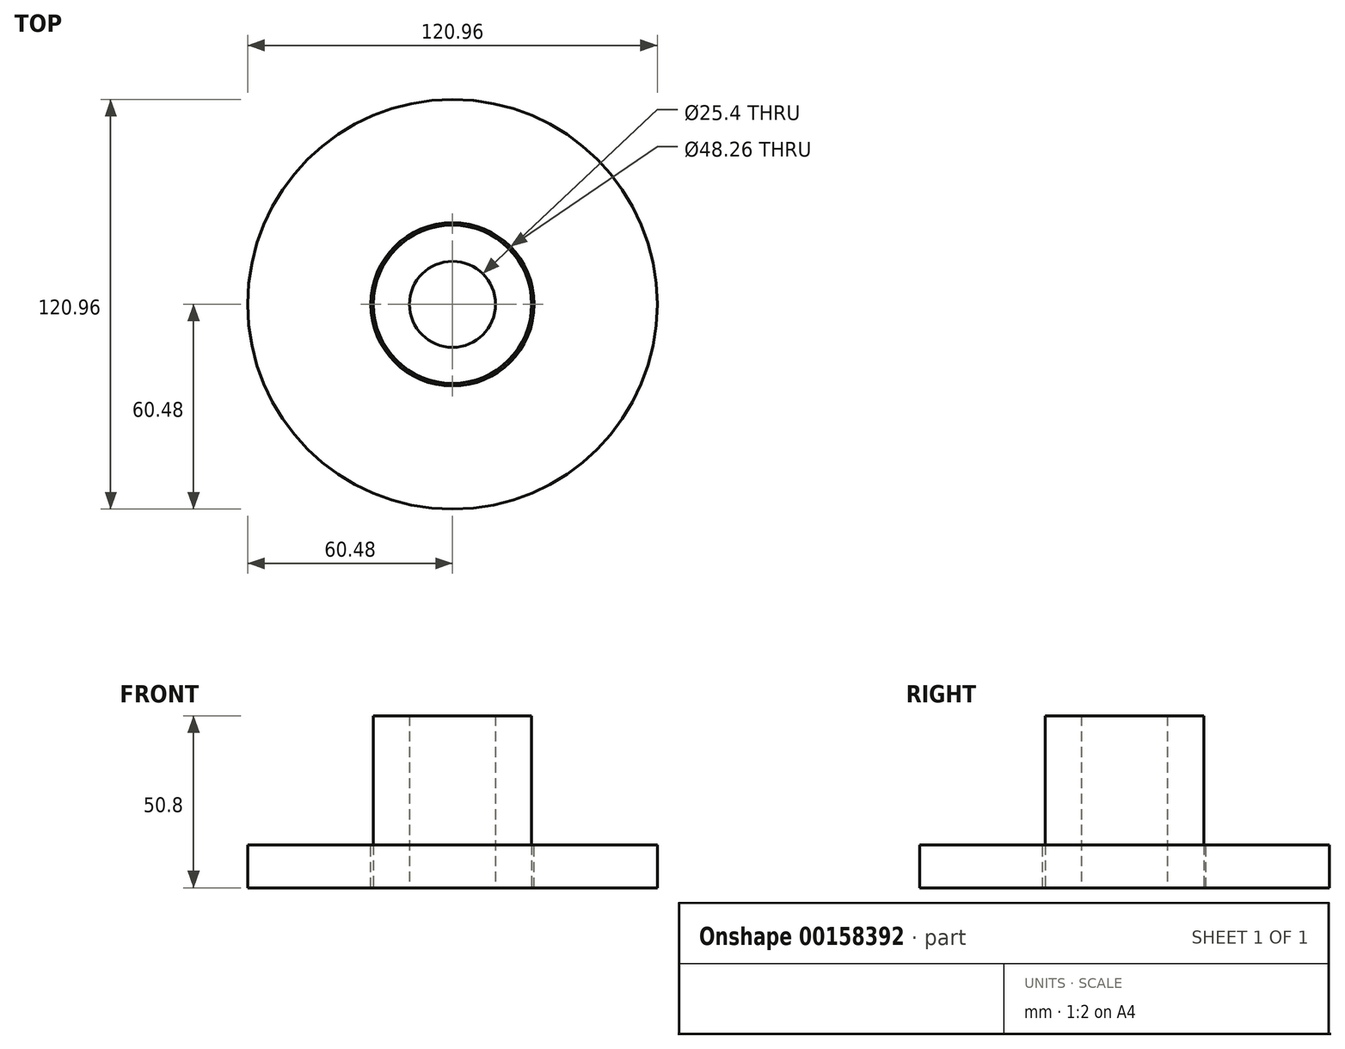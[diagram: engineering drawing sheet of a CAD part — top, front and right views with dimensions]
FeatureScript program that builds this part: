
annotation { "Feature Type Name" : "Feature", "Feature Type Description" : "" }
export const myFeature = defineFeature(function(context is Context, id is Id, definition is map)
    precondition{}
    {
        {
            var Q0;
            Q0=qCreatedBy(makeId("Top.planeOp"),FACE);
            var sketch = newSketch(context, id + "F0", { "sketchPlane" : qUnion([Q0])});
            skCircle(sketch, "E0", {"center": v(0, 0) * mm, "radius": 60.48 * mm});
            skSolve(sketch);
        }
        {
            var Q0;
            Q0 = qSketchRegion(id + "F0", true);
            extrude(context, id + "F1", {"entities" : qUnion([Q0]), "depth" : 12.7 * mm});
        }
        {
            var Q0;
            Q0=makeQuery(id+"F1.opExtrude","CAP_FACE",FACE,{"disambiguationData":[OSD([sQuery(id+"F0.wireOp",EDGE,"E0")])],"isStart":false});
            var sketch = newSketch(context, id + "F2", { "sketchPlane" : qUnion([Q0])});
            skCircle(sketch, "E1", {"center": v(0, 0) * mm, "radius": 8.5 * mm});
            skSolve(sketch);
        }
        {
            var Q0;
            Q0=sQuery(id+"F2.wireOp",VERTEX,"E1.center");
            var Q1;
            Q1=makeQuery(id+"F1.opExtrude","SWEPT_BODY",BODY,{"disambiguationData":[OSD([sQuery(id+"F0.wireOp",EDGE,"E0")])]});
            hole(context, id + "F3", {"style" : HoleStyle.SIMPLE, "endStyle" : HoleEndStyle.THROUGH, "holeDiameter" : 48.26 * mm, "locations" : qUnion([Q0]), "scope" : qUnion([Q1]), "isTappedThrough" : true});
        }
        {
            var Q0;
            Q0=qCreatedBy(makeId("Top.planeOp"),FACE);
            var sketch = newSketch(context, id + "F4", { "sketchPlane" : qUnion([Q0])});
            skCircle(sketch, "E2", {"center": v(0, 0) * mm, "radius": 23.39 * mm});
            skSolve(sketch);
        }
        {
            var Q0;
            Q0 = qSketchRegion(id + "F4", true);
            extrude(context, id + "F5", {"entities" : qUnion([Q0]), "depth" : 50.8 * mm});
        }
        {
            var Q0;
            Q0=qCreatedBy(makeId("Top.planeOp"),FACE);
            var sketch = newSketch(context, id + "F6", { "sketchPlane" : qUnion([Q0])});
            skCircle(sketch, "E3", {"center": v(0, 0) * mm, "radius": 13.03 * mm});
            skSolve(sketch);
        }
        {
            var Q0;
            Q0=sQuery(id+"F6.wireOp",VERTEX,"E3.center");
            var Q1;
            Q1=makeQuery(id+"F5.opExtrude","SWEPT_BODY",BODY,{"disambiguationData":[OSD([sQuery(id+"F4.wireOp",EDGE,"E2")])]});
            hole(context, id + "F7", {"style" : HoleStyle.SIMPLE, "endStyle" : HoleEndStyle.THROUGH, "oppositeDirection" : true, "holeDiameter" : 25.4 * mm, "locations" : qUnion([Q0]), "scope" : qUnion([Q1]), "isTappedThrough" : true});
        }
    });
